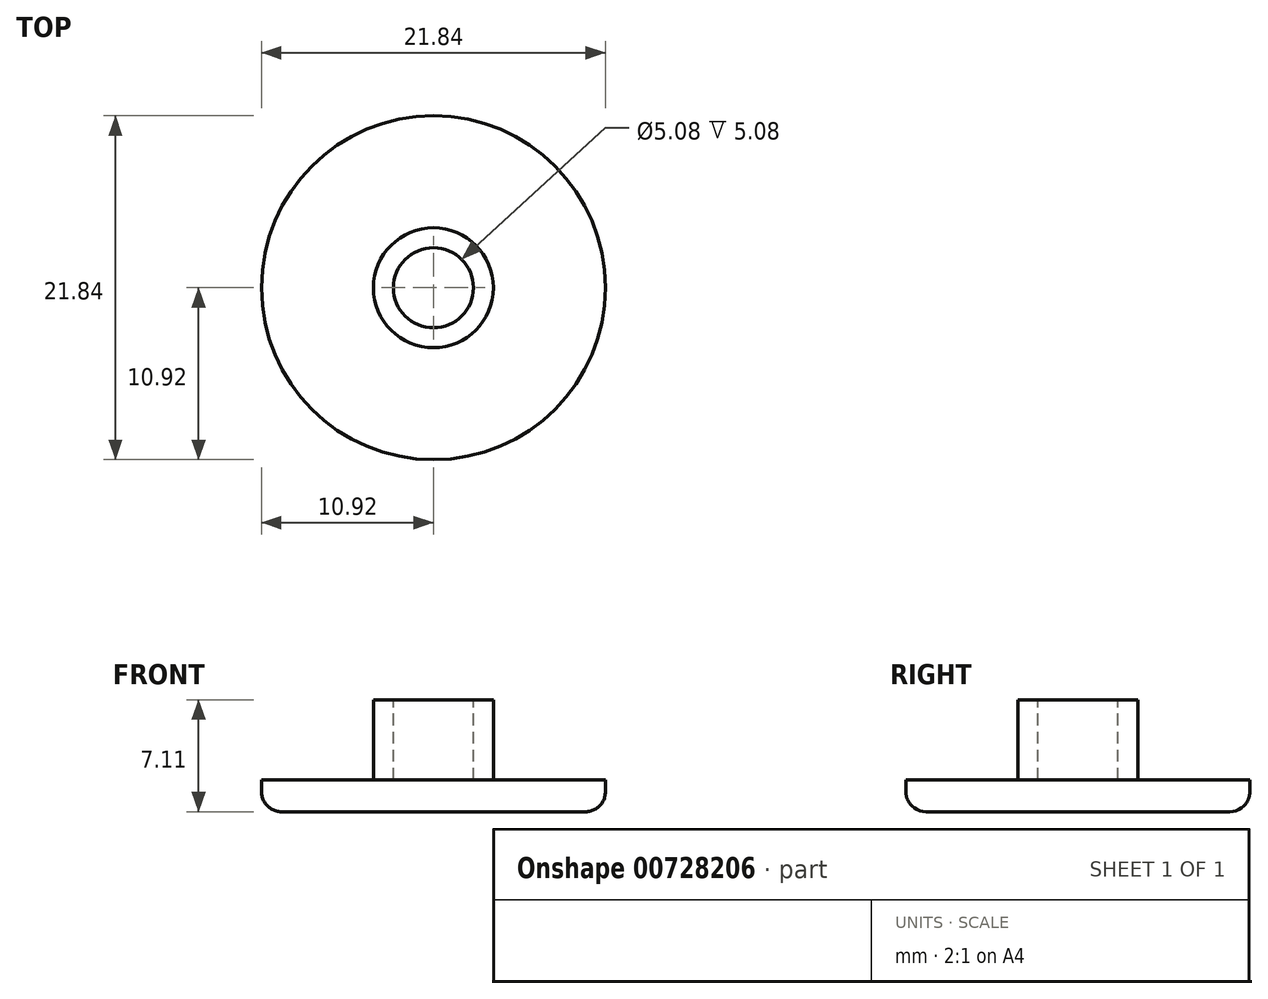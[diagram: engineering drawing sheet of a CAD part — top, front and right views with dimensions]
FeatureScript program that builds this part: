
annotation { "Feature Type Name" : "Feature", "Feature Type Description" : "" }
export const myFeature = defineFeature(function(context is Context, id is Id, definition is map)
    precondition{}
    {
        {
            var Q0;
            Q0=qCreatedBy(makeId("Top.planeOp"),FACE);
            var sketch = newSketch(context, id + "F0", { "sketchPlane" : qUnion([Q0])});
            skCircle(sketch, "E0", {"center": v(0, 0) * mm, "radius": 10.92 * mm});
            skSolve(sketch);
        }
        {
            var Q0;
            Q0=makeQuery(id+"F0.imprint","IMPRINT",FACE,{"disambiguationData":[TD([[makeQuery(id+"F0.imprint","IMPRINT",EDGE,{"derivedFrom":sQuery(id+"F0.wireOp",EDGE,"E0")}),1.0]])]});
            extrude(context, id + "F1", {"entities" : qUnion([Q0]), "depth" : 2.03 * mm, "offsetDistance" : 25.4 * mm});
        }
        {
            var Q0;
            Q0=makeQuery(id+"F1.opExtrude","CAP_FACE",FACE,{"disambiguationData":[OSD([sQuery(id+"F0.wireOp",EDGE,"E0")])],"isStart":false});
            var sketch = newSketch(context, id + "F2", { "sketchPlane" : qUnion([Q0])});
            skCircle(sketch, "E1", {"center": v(0, 0) * mm, "radius": 3.8 * mm});
            skSolve(sketch);
        }
        {
            var Q0;
            Q0 = qSketchRegion(id + "F2", true);
            extrude(context, id + "F3", {"entities" : qUnion([Q0]), "operationType" : NewBodyOperationType.ADD, "depth" : 5.08 * mm, "offsetDistance" : 25.4 * mm});
        }
        {
            var Q0;
            Q0=makeQuery(id+"F3.opExtrude","CAP_FACE",FACE,{"disambiguationData":[OSD([sQuery(id+"F2.wireOp",EDGE,"E1")])],"isStart":false});
            var sketch = newSketch(context, id + "F4", { "sketchPlane" : qUnion([Q0])});
            skCircle(sketch, "E2", {"center": v(0, 0) * mm, "radius": 2.54 * mm});
            skSolve(sketch);
        }
        {
            var Q0;
            Q0=makeQuery(id+"F4.imprint","IMPRINT",FACE,{"disambiguationData":[TD([[makeQuery(id+"F4.imprint","IMPRINT",EDGE,{"derivedFrom":sQuery(id+"F4.wireOp",EDGE,"E2")}),1.0]])]});
            var Q1;
            Q1=makeQuery(id+"F1.opExtrude","CAP_FACE",FACE,{"disambiguationData":[OSD([sQuery(id+"F0.wireOp",EDGE,"E0")])],"isStart":false});
            extrude(context, id + "F5", {"entities" : qUnion([Q0]), "operationType" : NewBodyOperationType.REMOVE, "endBound" : BoundingType.UP_TO_SURFACE, "oppositeDirection" : true, "depth" : 25.4 * mm, "endBoundEntityFace" : qUnion([Q1]), "offsetDistance" : 25.4 * mm});
        }
        {
            var Q0;
            Q0=makeQuery(id+"F1.opExtrude","CAP_FACE",FACE,{"disambiguationData":[OSD([sQuery(id+"F0.wireOp",EDGE,"E0")])],"isStart":true});
            fillet(context, id + "F6", {"entities" : qUnion([Q0]), "radius" : 1.27 * mm, "tangentPropagation" : true, "allowEdgeOverflow" : false});
        }
    });
